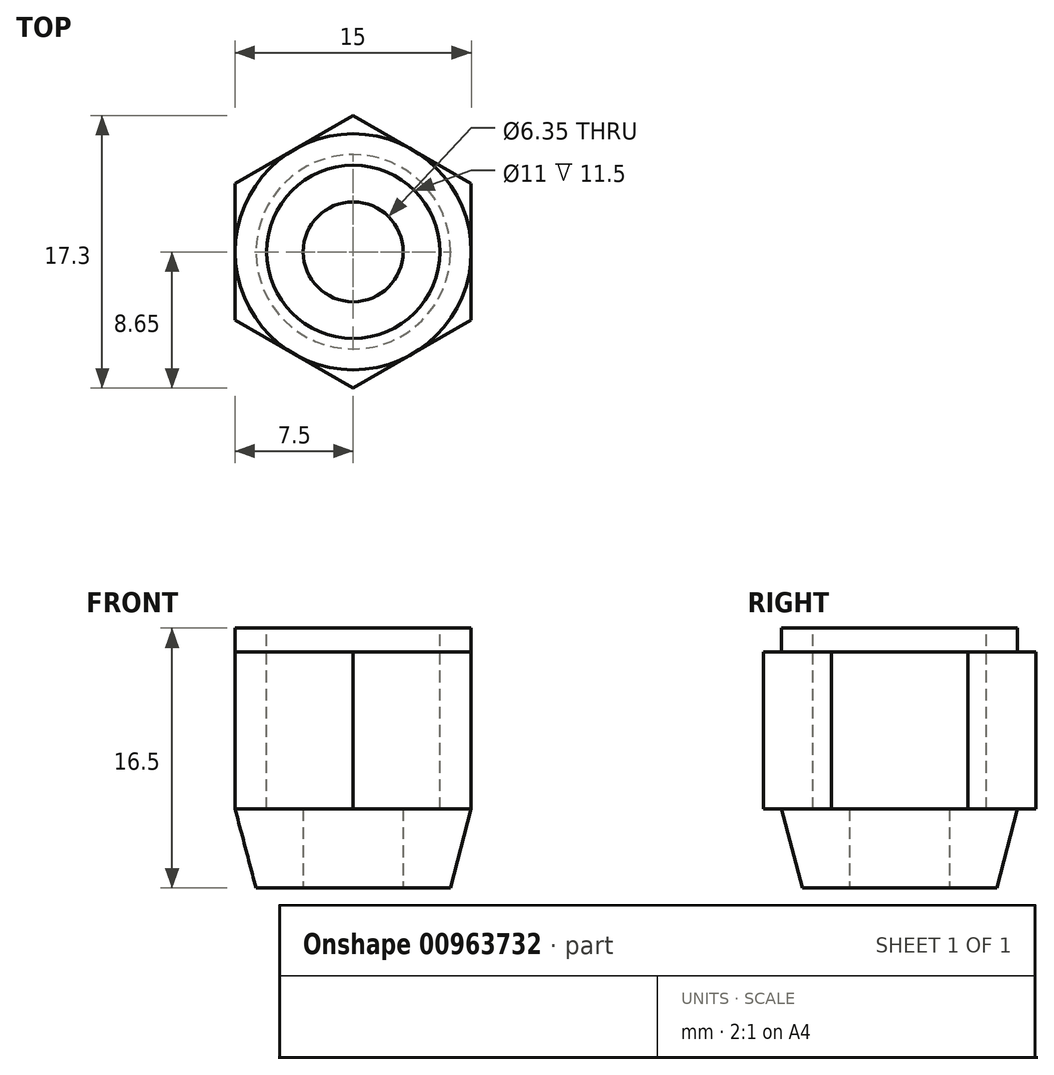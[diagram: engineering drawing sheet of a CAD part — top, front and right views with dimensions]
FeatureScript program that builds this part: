
annotation { "Feature Type Name" : "Feature", "Feature Type Description" : "" }
export const myFeature = defineFeature(function(context is Context, id is Id, definition is map)
    precondition{}
    {
        {
            var Q0;
            Q0=qCreatedBy(makeId("Front.planeOp"),FACE);
            var sketch = newSketch(context, id + "F0", { "sketchPlane" : qUnion([Q0])});
            skLineSegment(sketch, "E0", {"start": v(0, 0) * mm, "end": v(3.18, 0) * mm});
            skLineSegment(sketch, "E1", {"start": v(3.18, 0) * mm, "end": v(6.18, 0) * mm});
            skLineSegment(sketch, "E2", {"start": v(3.18, 0) * mm, "end": v(3.18, 5) * mm});
            skLineSegment(sketch, "E3", {"start": v(3.18, 5) * mm, "end": v(7.5, 5) * mm});
            skLineSegment(sketch, "E4", {"start": v(7.5, 5) * mm, "end": v(6.17, 0) * mm});
            skLineSegment(sketch, "E5", {"start": v(0, 0) * mm, "end": v(0, 3.6) * mm, "construction": true});
            skSolve(sketch);
        }
        {
            var Q0;
            Q0=makeQuery(id+"F0.imprint","IMPRINT",FACE,{"disambiguationData":[TD([[makeQuery(id+"F0.imprint","IMPRINT",EDGE,{"derivedFrom":sQuery(id+"F0.wireOp",EDGE,"E1")}),1.0]])]});
            var Q1;
            Q1=sQuery(id+"F0.wireOp",EDGE,"E5");
            revolve(context, id + "F1", {"surfaceOperationType" : NewSurfaceOperationType.NEW, "entities" : qUnion([Q0]), "axis" : qUnion([Q1]), "revolveType" : RevolveType.FULL});
        }
        {
            var Q0;
            Q0=makeQuery(id+"F1.opRevolve","SWEPT_FACE",FACE,{"disambiguationData":[OSD([sQuery(id+"F0.wireOp",EDGE,"E3")])]});
            var sketch = newSketch(context, id + "F2", { "sketchPlane" : qUnion([Q0])});
            skCircle(sketch, "E6.cCircle", {"center": v(0, 0) * mm, "radius": 7.5 * mm, "construction": true});
            skLineSegment(sketch, "E6.0", {"start": v(7.5, 4.33) * mm, "end": v(7.5, -4.33) * mm});
            skLineSegment(sketch, "E6.1", {"start": v(7.5, -4.33) * mm, "end": v(0, -8.65) * mm});
            skLineSegment(sketch, "E6.2", {"start": v(0, -8.65) * mm, "end": v(-7.5, -4.33) * mm});
            skLineSegment(sketch, "E6.3", {"start": v(-7.5, -4.33) * mm, "end": v(-7.5, 4.33) * mm});
            skLineSegment(sketch, "E6.4", {"start": v(-7.5, 4.33) * mm, "end": v(0, 8.65) * mm});
            skLineSegment(sketch, "E6.5", {"start": v(0, 8.65) * mm, "end": v(7.5, 4.33) * mm});
            skPoint(sketch, "E6.0.midPoint", {"position": v(7.5, 0) * mm});
            skSolve(sketch);
        }
        {
            var Q0;
            {var subQ0=sQuery(id+"F2.wireOp",EDGE,"E6.2");var subQ1=sQuery(id+"F2.wireOp",EDGE,"E6.1");var subQ2=makeQuery(id+"F2.imprint","INTERSECT",VERTEX,{"derivedFrom":[subQ1,subQ0]});Q0=makeQuery(id+"F2.imprint","IMPRINT",FACE,{"disambiguationData":[TD([[makeQuery(id+"F2.imprint","IMPRINT",EDGE,{"disambiguationData":[TD([[subQ2,1.0]])],"derivedFrom":subQ1}),-1.0]])]});}
            var Q1;
            {var subQ0=sQuery(id+"F2.wireOp",EDGE,"E6.1");var subQ1=sQuery(id+"F2.wireOp",EDGE,"E6.0");var subQ2=makeQuery(id+"F2.imprint","INTERSECT",VERTEX,{"derivedFrom":[subQ1,subQ0]});Q1=makeQuery(id+"F2.imprint","IMPRINT",FACE,{"disambiguationData":[TD([[makeQuery(id+"F2.imprint","IMPRINT",EDGE,{"disambiguationData":[TD([[subQ2,1.0]])],"derivedFrom":subQ1}),-1.0]])]});}
            var Q2;
            {var subQ0=sQuery(id+"F2.wireOp",EDGE,"E6.5");var subQ1=sQuery(id+"F2.wireOp",EDGE,"E6.0");var subQ2=makeQuery(id+"F2.imprint","INTERSECT",VERTEX,{"derivedFrom":[subQ1,subQ0]});Q2=makeQuery(id+"F2.imprint","IMPRINT",FACE,{"disambiguationData":[TD([[makeQuery(id+"F2.imprint","IMPRINT",EDGE,{"disambiguationData":[TD([[subQ2,-1.0]])],"derivedFrom":subQ1}),-1.0]])]});}
            var Q3;
            {var subQ0=sQuery(id+"F2.wireOp",EDGE,"E6.5");var subQ1=sQuery(id+"F2.wireOp",EDGE,"E6.4");var subQ2=makeQuery(id+"F2.imprint","INTERSECT",VERTEX,{"derivedFrom":[subQ1,subQ0]});Q3=makeQuery(id+"F2.imprint","IMPRINT",FACE,{"disambiguationData":[TD([[makeQuery(id+"F2.imprint","IMPRINT",EDGE,{"disambiguationData":[TD([[subQ2,1.0]])],"derivedFrom":subQ1}),-1.0]])]});}
            var Q4;
            {var subQ0=sQuery(id+"F2.wireOp",EDGE,"E6.4");var subQ1=sQuery(id+"F2.wireOp",EDGE,"E6.3");var subQ2=makeQuery(id+"F2.imprint","INTERSECT",VERTEX,{"derivedFrom":[subQ1,subQ0]});Q4=makeQuery(id+"F2.imprint","IMPRINT",FACE,{"disambiguationData":[TD([[makeQuery(id+"F2.imprint","IMPRINT",EDGE,{"disambiguationData":[TD([[subQ2,1.0]])],"derivedFrom":subQ1}),-1.0]])]});}
            var Q5;
            {var subQ0=sQuery(id+"F2.wireOp",EDGE,"E6.3");var subQ1=sQuery(id+"F2.wireOp",EDGE,"E6.2");var subQ2=makeQuery(id+"F2.imprint","INTERSECT",VERTEX,{"derivedFrom":[subQ1,subQ0]});Q5=makeQuery(id+"F2.imprint","IMPRINT",FACE,{"disambiguationData":[TD([[makeQuery(id+"F2.imprint","IMPRINT",EDGE,{"disambiguationData":[TD([[subQ2,1.0]])],"derivedFrom":subQ1}),-1.0]])]});}
            var Q6;
            {var subQ0=sQuery(id+"F0.wireOp",EDGE,"E3");Q6=makeQuery(id+"F2.imprint","IMPRINT",FACE,{"disambiguationData":[TD([[makeQuery(id+"F2.imprint","IMPRINT",EDGE,{"derivedFrom":makeQuery(id+"F1.opRevolve","SWEPT_EDGE",EDGE,{"disambiguationData":[OSD([sQuery(id+"F0.wireOp",EDGE,"E2"),subQ0])]})}),1.0]])]});}
            extrude(context, id + "F3", {"entities" : qUnion([Q0, Q1, Q2, Q3, Q4, Q5, Q6]), "operationType" : NewBodyOperationType.ADD, "depth" : 10 * mm, "offsetDistance" : 25 * mm});
        }
        {
            var Q0;
            Q0=makeQuery(id+"F3.opExtrude","CAP_FACE",FACE,{"disambiguationData":[OSD([sQuery(id+"F0.wireOp",EDGE,"E2"),sQuery(id+"F0.wireOp",EDGE,"E3"),sQuery(id+"F2.wireOp",EDGE,"E6.0"),sQuery(id+"F2.wireOp",EDGE,"E6.1"),sQuery(id+"F2.wireOp",EDGE,"E6.2"),sQuery(id+"F2.wireOp",EDGE,"E6.3"),sQuery(id+"F2.wireOp",EDGE,"E6.4"),sQuery(id+"F2.wireOp",EDGE,"E6.5")])],"isStart":false});
            var sketch = newSketch(context, id + "F4", { "sketchPlane" : qUnion([Q0])});
            skCircle(sketch, "E7", {"center": v(0, 0) * mm, "radius": 7.5 * mm});
            skSolve(sketch);
        }
        {
            var Q0;
            Q0=makeQuery(id+"F4.imprint","IMPRINT",FACE,{"disambiguationData":[TD([[makeQuery(id+"F4.imprint","IMPRINT",EDGE,{"derivedFrom":makeQuery(id+"F3.opExtrude","CAP_EDGE",EDGE,{"disambiguationData":[OSD([sQuery(id+"F0.wireOp",EDGE,"E2"),sQuery(id+"F0.wireOp",EDGE,"E3")])],"isStart":false})}),1.0]])]});
            extrude(context, id + "F5", {"entities" : qUnion([Q0]), "operationType" : NewBodyOperationType.ADD, "depth" : 1.5 * mm, "offsetDistance" : 25 * mm});
        }
        {
            var Q0;
            Q0=makeQuery(id+"F5.opExtrude","CAP_FACE",FACE,{"disambiguationData":[OSD([sQuery(id+"F0.wireOp",EDGE,"E2"),sQuery(id+"F0.wireOp",EDGE,"E3"),sQuery(id+"F4.wireOp",EDGE,"E7")])],"isStart":false});
            var sketch = newSketch(context, id + "F6", { "sketchPlane" : qUnion([Q0])});
            skCircle(sketch, "E8", {"center": v(0, 0) * mm, "radius": 5.5 * mm});
            skSolve(sketch);
        }
        {
            var Q0;
            Q0=makeQuery(id+"F6.imprint","IMPRINT",FACE,{"disambiguationData":[TD([[makeQuery(id+"F6.imprint","IMPRINT",EDGE,{"derivedFrom":sQuery(id+"F6.wireOp",EDGE,"E8")}),1.0]])]});
            extrude(context, id + "F7", {"entities" : qUnion([Q0]), "operationType" : NewBodyOperationType.REMOVE, "oppositeDirection" : true, "depth" : 11.5 * mm, "offsetDistance" : 25 * mm});
        }
    });
